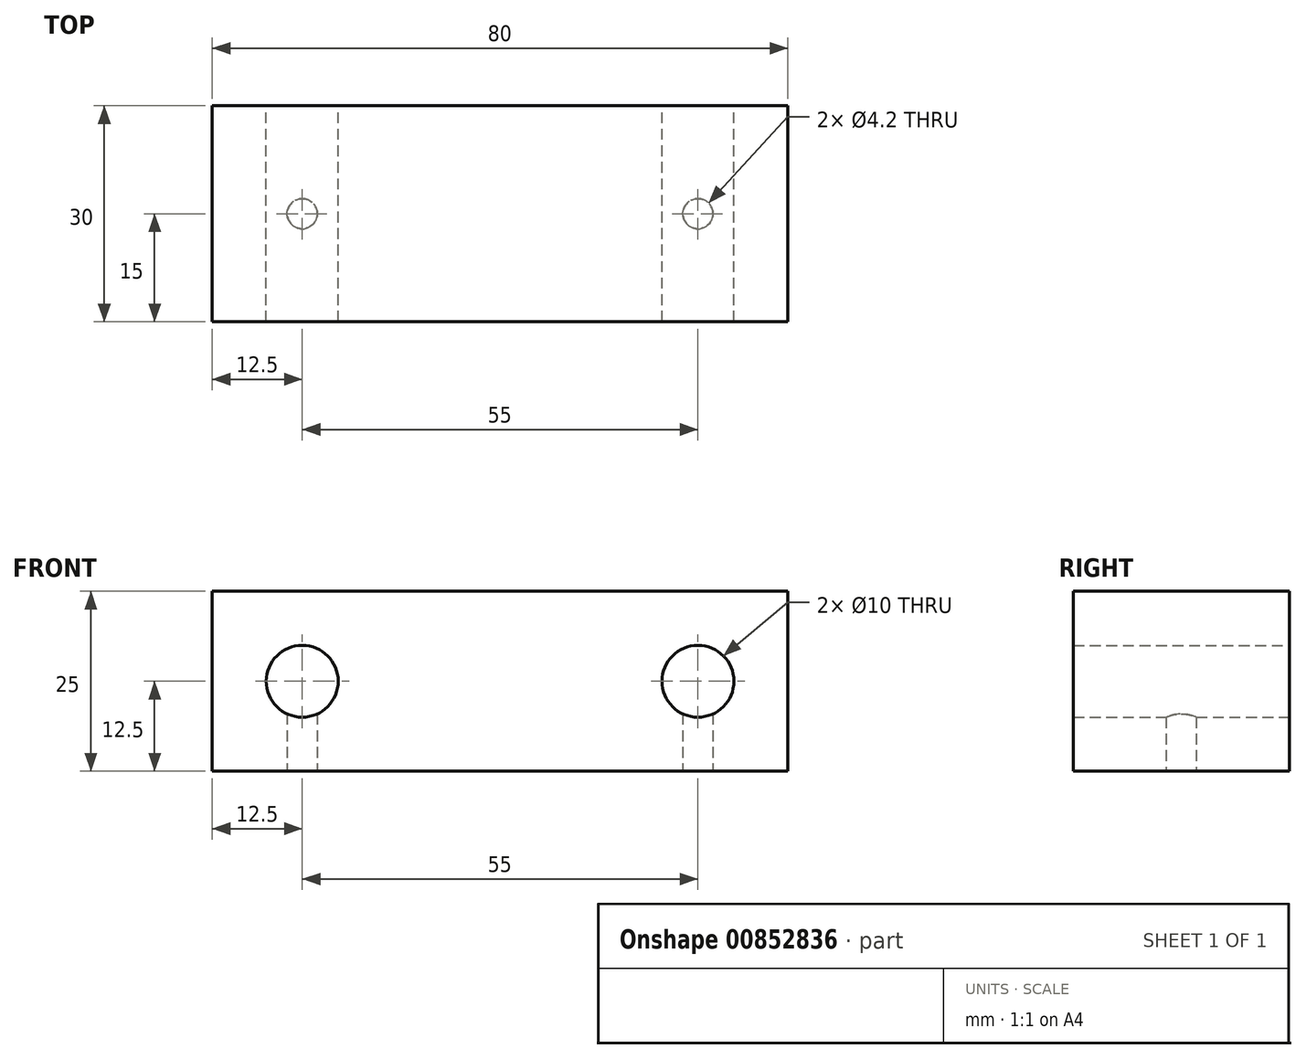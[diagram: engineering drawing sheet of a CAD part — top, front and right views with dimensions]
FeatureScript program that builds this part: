
annotation { "Feature Type Name" : "Feature", "Feature Type Description" : "" }
export const myFeature = defineFeature(function(context is Context, id is Id, definition is map)
    precondition{}
    {
        {
            var Q0;
            Q0=qCreatedBy(makeId("Front.planeOp"),FACE);
            var sketch = newSketch(context, id + "F0", { "sketchPlane" : qUnion([Q0])});
            skLineSegment(sketch, "E0.bottom", {"start": v(40, 12.5) * mm, "end": v(-40, 12.5) * mm});
            skLineSegment(sketch, "E0.top", {"start": v(40, -12.5) * mm, "end": v(-40, -12.5) * mm});
            skLineSegment(sketch, "E0.left", {"start": v(40, 12.5) * mm, "end": v(40, -12.5) * mm});
            skLineSegment(sketch, "E0.right", {"start": v(-40, 12.5) * mm, "end": v(-40, -12.5) * mm});
            skPoint(sketch, "E0.middle", {"position": v(0, 0) * mm});
            skCircle(sketch, "E1", {"center": v(-27.5, 0) * mm, "radius": 5 * mm});
            skCircle(sketch, "E2", {"center": v(27.5, 0) * mm, "radius": 5 * mm});
            skLineSegment(sketch, "E3", {"start": v(-27.5, 0) * mm, "end": v(27.5, 0) * mm, "construction": true});
            skSolve(sketch);
        }
        {
            var Q0;
            Q0 = qSketchRegion(id + "F0", true);
            extrude(context, id + "F1", {"entities" : qUnion([Q0]), "endBound" : BoundingType.SYMMETRIC, "depth" : 30 * mm, "offsetDistance" : 25 * mm, "hasSecondDirection" : true, "secondDirectionOppositeDirection" : true, "secondDirectionDepth" : 25 * mm});
        }
        {
            var Q0;
            Q0=makeQuery(id+"F1.opExtrude","SWEPT_FACE",FACE,{"disambiguationData":[OSD([sQuery(id+"F0.wireOp",EDGE,"E0.top")])]});
            var sketch = newSketch(context, id + "F2", { "sketchPlane" : qUnion([Q0])});
            skLineSegment(sketch, "E4", {"start": v(-27.5, 0) * mm, "end": v(27.5, 0) * mm, "construction": true});
            skSolve(sketch);
        }
        {
            var Q0;
            Q0=sQuery(id+"F2.wireOp",VERTEX,"E4.start");
            var Q1;
            Q1=sQuery(id+"F2.wireOp",VERTEX,"E4.end");
            var Q2;
            Q2=makeQuery(id+"F1.opExtrude","SWEPT_BODY",BODY,{"disambiguationData":[OSD([sQuery(id+"F0.wireOp",EDGE,"E0.bottom"),sQuery(id+"F0.wireOp",EDGE,"E0.top"),sQuery(id+"F0.wireOp",EDGE,"E0.left"),sQuery(id+"F0.wireOp",EDGE,"E0.right"),sQuery(id+"F0.wireOp",EDGE,"E1"),sQuery(id+"F0.wireOp",EDGE,"E2")])]});
            hole(context, id + "F3", {"style" : HoleStyle.SIMPLE, "endStyle" : HoleEndStyle.BLIND, "standardTappedOrClearance" : lookupTablePath({ "standard" : "ISO", "engagement" : "75%", "pitch" : "0.8 mm", "size" : "M5", "type" : "Tapped" }), "standardBlindInLast" : lookupTablePath({ "standard" : "ISO", "engagement" : "75%", "pitch" : "0.8 mm", "size" : "M5", "type" : "Tapped" }), "holeDiameter" : 4.2 * mm, "majorDiameter" : 5 * mm, "showTappedDepth" : true, "holeDepth" : 14.4 * mm, "isTappedThrough" : true, "tappedDepth" : 12 * mm, "tapClearance" : 3, "locations" : qUnion([Q0, Q1]), "scope" : qUnion([Q2])});
        }
    });
